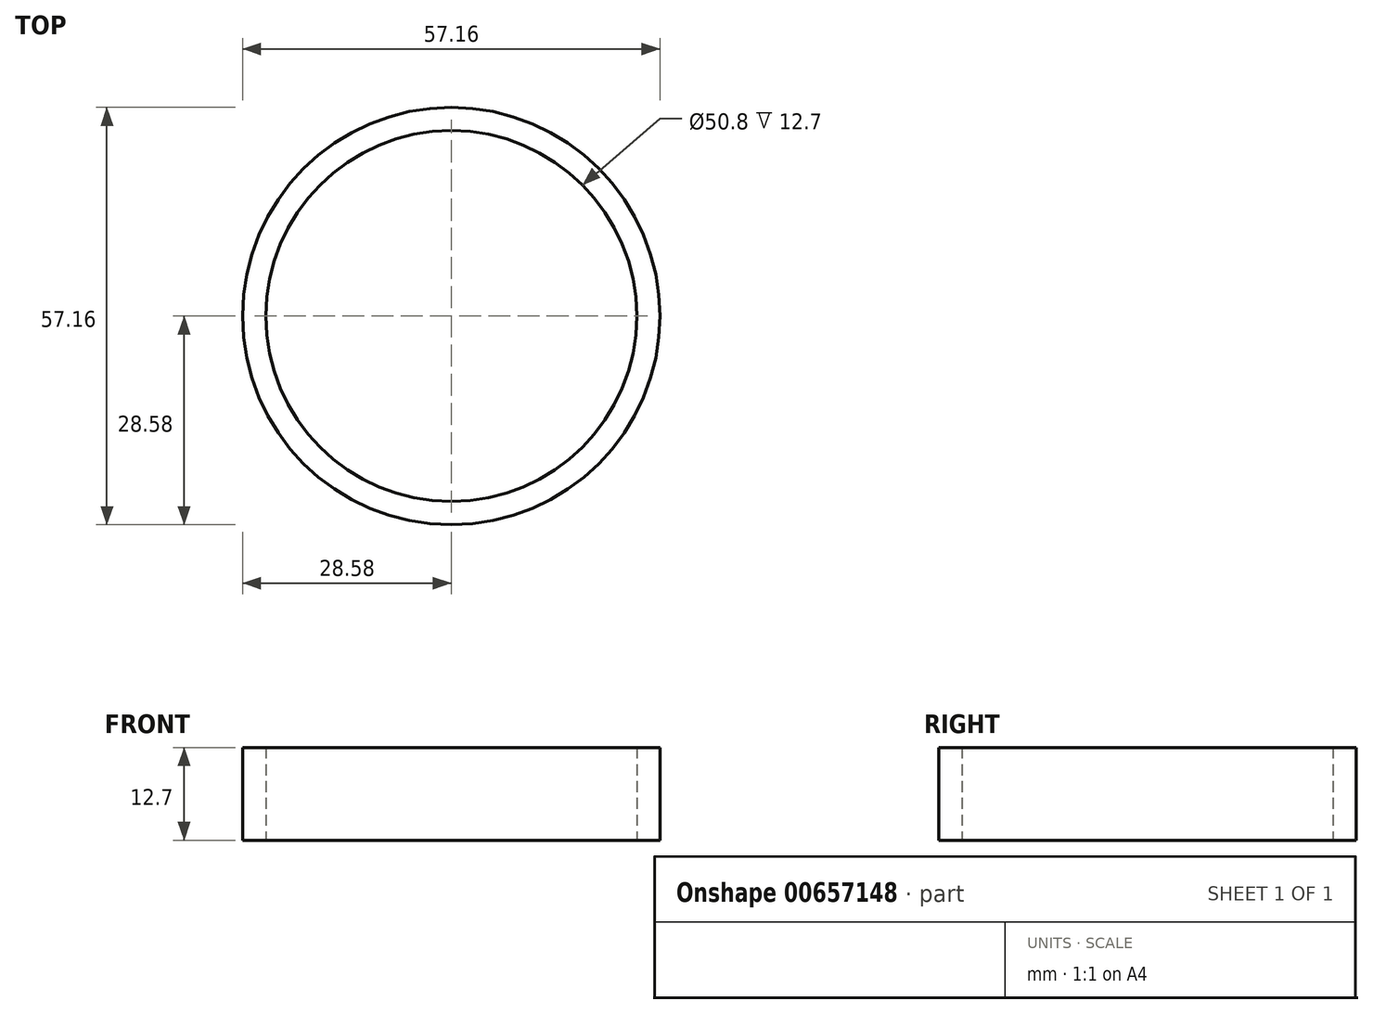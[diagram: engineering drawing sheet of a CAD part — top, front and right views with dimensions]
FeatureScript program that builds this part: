
annotation { "Feature Type Name" : "Feature", "Feature Type Description" : "" }
export const myFeature = defineFeature(function(context is Context, id is Id, definition is map)
    precondition{}
    {
        {
            var Q0;
            Q0=qCreatedBy(makeId("Top.planeOp"),FACE);
            var sketch = newSketch(context, id + "F0", { "sketchPlane" : qUnion([Q0])});
            skCircle(sketch, "E0", {"center": v(0, 0) * mm, "radius": 25.4 * mm});
            skCircle(sketch, "E1", {"center": v(0, 0) * mm, "radius": 28.58 * mm});
            skSolve(sketch);
        }
        {
            var Q0;
            Q0=qCreatedBy(makeId("Top.planeOp"),FACE);
            var sketch = newSketch(context, id + "F1", { "sketchPlane" : qUnion([Q0])});
            skLineSegment(sketch, "E2.bottom", {"start": v(0, 12.88) * mm, "end": v(115.89, 12.88) * mm});
            skLineSegment(sketch, "E2.top", {"start": v(0, -12.52) * mm, "end": v(115.89, -12.52) * mm});
            skLineSegment(sketch, "E2.left", {"start": v(0, 12.88) * mm, "end": v(0, -12.52) * mm});
            skLineSegment(sketch, "E2.right", {"start": v(115.89, 12.88) * mm, "end": v(115.89, -12.52) * mm});
            skSolve(sketch);
        }
        {
            var Q0;
            Q0 = qSketchRegion(id + "F0", true);
            extrude(context, id + "F2", {"entities" : qUnion([Q0]), "depth" : 12.7 * mm, "offsetDistance" : 25.4 * mm});
        }
    });
